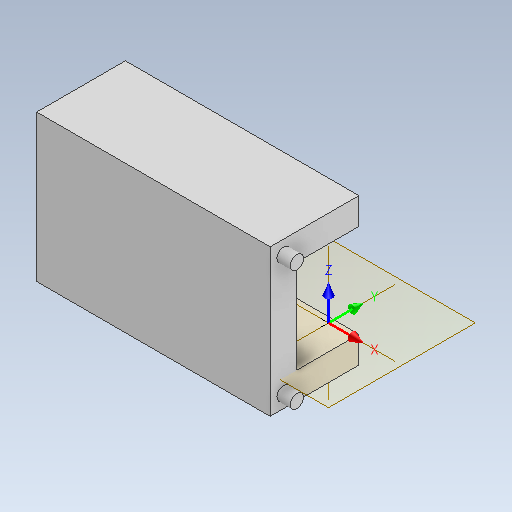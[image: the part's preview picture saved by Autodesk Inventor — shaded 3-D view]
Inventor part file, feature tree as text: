
AUTODESK INVENTOR PART (.ipt)
format: ipt  version: 2025.2 (Build 292293000, 293)  size: 429,056 bytes
history: native  units: mm
features: sketch x26, revolve x16, other x9, extrude x7, fillet x2, plane x1, hole x1
ambient origin geometry x8: Origin, YZ Plane, XZ Plane, XY Plane, X Axis, Y Axis, Z Axis, Center Point
bodies: Volumenkörper2 (feature_tree), Volumenkörper3 (feature_tree)
feature tree (62):
  sketch  "Skizze1"  dims[d0=0.0mm d1=0.0mm d2=0.0mm d3=0.0mm d4=0.0mm d5=0.0mm d13=29.5mm d14=18.6mm d16=0.0mm d17=14.0mm]
  other  "BKS1"
  plane  "Arbeitsebene1"
  sketch  "Skizze5"  dims[d22=2.0mm d23=2.0mm]
  revolve  "Umdrehung2"
  revolve  "Umdrehung3"
  revolve  "Umdrehung4"
  revolve  "Umdrehung5"
  revolve  "Umdrehung6"
  revolve  "Umdrehung7"
  revolve  "Umdrehung8"
  revolve  "Umdrehung9"
  revolve  "Umdrehung10"
  revolve  "Umdrehung11"
  revolve  "Umdrehung12"
  revolve  "Umdrehung13"
  revolve  "Umdrehung14"
  revolve  "Umdrehung15"
  revolve  "Umdrehung16"
  revolve  "Umdrehung17"
  extrude  "Extrusion3"  Depth=14.0mm TaperAngle=0.0deg
  other  "Kombinieren1"
  extrude  "Extrusion9"  Depth=15.0mm
  extrude  "Extrusion10"  Depth=2.0mm
  extrude  "Extrusion11"  Depth=2.0mm
  extrude  "Extrusion12"  TaperAngle=360.0deg  [1 undecoded]
  extrude  "Extrusion13"  TaperAngle=360.0deg  [1 undecoded]
  hole  "Bohrung1"  [1 undecoded]
  sketch  "Skizze6"  dims[d24=2.0mm d25=2.0mm]
  sketch  "Skizze7"  dims[d26=360.0deg d27=360.0deg]
  sketch  "Skizze8"  dims[d28=360.0deg d29=360.0deg]
  sketch  "Skizze9"  dims[d30=360.0deg d31=360.0deg]
  sketch  "Skizze10"  dims[d32=360.0deg d33=360.0deg d34=360.0deg d35=360.0deg]
  sketch  "Skizze11"  dims[d36=360.0deg]
  sketch  "Skizze12"  dims[d37=360.0deg]
  sketch  "Skizze13"  dims[d38=360.0deg]
  sketch  "Skizze14"  dims[d39=360.0deg]
  sketch  "Skizze15"  dims[d40=360.0deg]
  sketch  "Skizze16"  dims[d41=360.0deg]
  sketch  "Skizze17"  dims[d42=35.0mm d43=0.0mm]
  sketch  "Skizze18"  dims[d52=4.0mm]
  sketch  "Skizze19"  dims[d53=4.0mm]
  sketch  "Skizze20"  dims[d54=4.0mm]
  sketch  "Skizze21"  dims[d55=4.0mm]
  sketch  "Skizze22"  dims[d62=2.0mm d63=0.0mm]
  sketch  "Skizze29"  dims[d64=2.0mm d65=0.0mm]
  sketch  "Skizze30"  dims[d66=2.0mm d67=0.0mm]
  sketch  "Skizze31"  dims[d68=2.0mm d69=0.0mm]
  sketch  "Skizze32"  dims[d70=2.0mm]
  sketch  "Skizze33"  dims[d71=2.0mm]
  sketch  "Skizze34"  dims[d73=2.0mm d74=2.0mm d76=2.0mm d77=2.0mm d80=2.0mm d82=2.0mm d83=2.0mm d84=2.0mm d85=2.0mm d86=2.0mm d87=40.0mm d88=0.0mm d90=2.5mm d91=6.0mm d92=4.0mm d93=2.0mm d94=90.0deg d95=2.5mm d96=0.0mm d97=5.0mm d98=2.0mm d99=5.0mm d100=2.0mm d101=2.0mm d102=2.0mm d103=2.0mm d104=2.0mm d105=18.6mm d106=26.6mm d107=9.3mm d108=9.3mm d109=22.0mm]
  other  "BKS1: YZ-Ebene"
  other  "BKS1: XZ-Ebene"
  other  "BKS1: XY-Ebene"
  other  "BKS1: X-Achse"
  other  "BKS1: Y-Achse"
  other  "BKS1: Z-Achse"
  other  "BKS1: Mittelpunkt"
  sketch  "Skizze3"  dims[d18=15.0mm d19=5.0mm]
  extrude  "Extrusion2"  TaperAngle=360.0deg  [1 undecoded]
  fillet  "Rundung4"  [1 undecoded]
  fillet  "Rundung3"  [1 undecoded]
note: 6 required parameter values undecoded (feature->parameter linkage not recoverable at this tier; creation-order binding heuristic only, values carry confidence <= 0.55)
